# Revit family: V_Enave_CT_150_200_P_Eng
name_source: partatom
category: Mechanical Equipment
units: mm (PartAtom-declared; Revit-internal decimal feet)

## family parameters
Always vertical = Yes
Classification = None
Cut with Voids When Loaded = No
Part Type = Normal
Room Calculation Point = No
Round Connector Dimension = Use Diameter
Shared = No
Work Plane-Based = No

## types (4) — shared parameters
00_20_Manufacturer = Vents
00_20_Name = Air handling units
Amperage = 1 A
Casing Material = EPP
Diameter = 160 mm  [stored 0.524934 ft]
Filter = G4 / Coarse > 60%
H = 242 mm  [stored 0.793963 ft]
Height = 242 mm  [stored 0.793963 ft]
L = 1160 mm  [stored 3.80577 ft]
L1 = 685 mm
L2 = 1246 mm  [stored 4.08793 ft]
Length = 1160 mm  [stored 3.80577 ft]
Load Classification = HVAC
Maintenance zone material = <By Category>
Manufacturer = Vents
Number of Fase = 1
Voltage = 230 V
W = 683 mm  [stored 2.24081 ft]
W1 = 642 mm  [stored 2.1063 ft]
W2 = 610 mm  [stored 2.00131 ft]
W3 = 523 mm
Width = 610 mm  [stored 2.00131 ft]
e = 151 mm  [stored 0.495407 ft]
h1 = 94 mm  [stored 0.308399 ft]
⌀D = 160 mm  [stored 0.524934 ft]
⌀D1 = 125 mm  [stored 0.410105 ft]
zero-valued in all types: Default Elevation

## per-type parameters (varying)
| type | Maximum Air Flow | Power | Sound pressure level at 3 m distance | Weight |
| Enave-C 150/151 | 229.0 m³/h | 96 W | 27 дБА | 18.00 kg |
| Enave-CT 150/151 | 229.0 m³/h | 96 W | 27 дБА | 19.50 kg |
| Enave-C 200/201 | 279.0 m³/h | 135 W | 33 дБА | 18.00 kg |
| Enave-CT 200/201 | 279.0 m³/h | 135 W | 33 дБА | 19.50 kg |

note: column(s) folded — value = type name in every type: 00_20_Type

note: [stored X ft] marks values corroborated as IEEE doubles in the binary element streams (Revit-internal decimal feet)

## geometry (parser evidence)
native form markers: Sweep x14
no freeform markers — native parametric forms only
